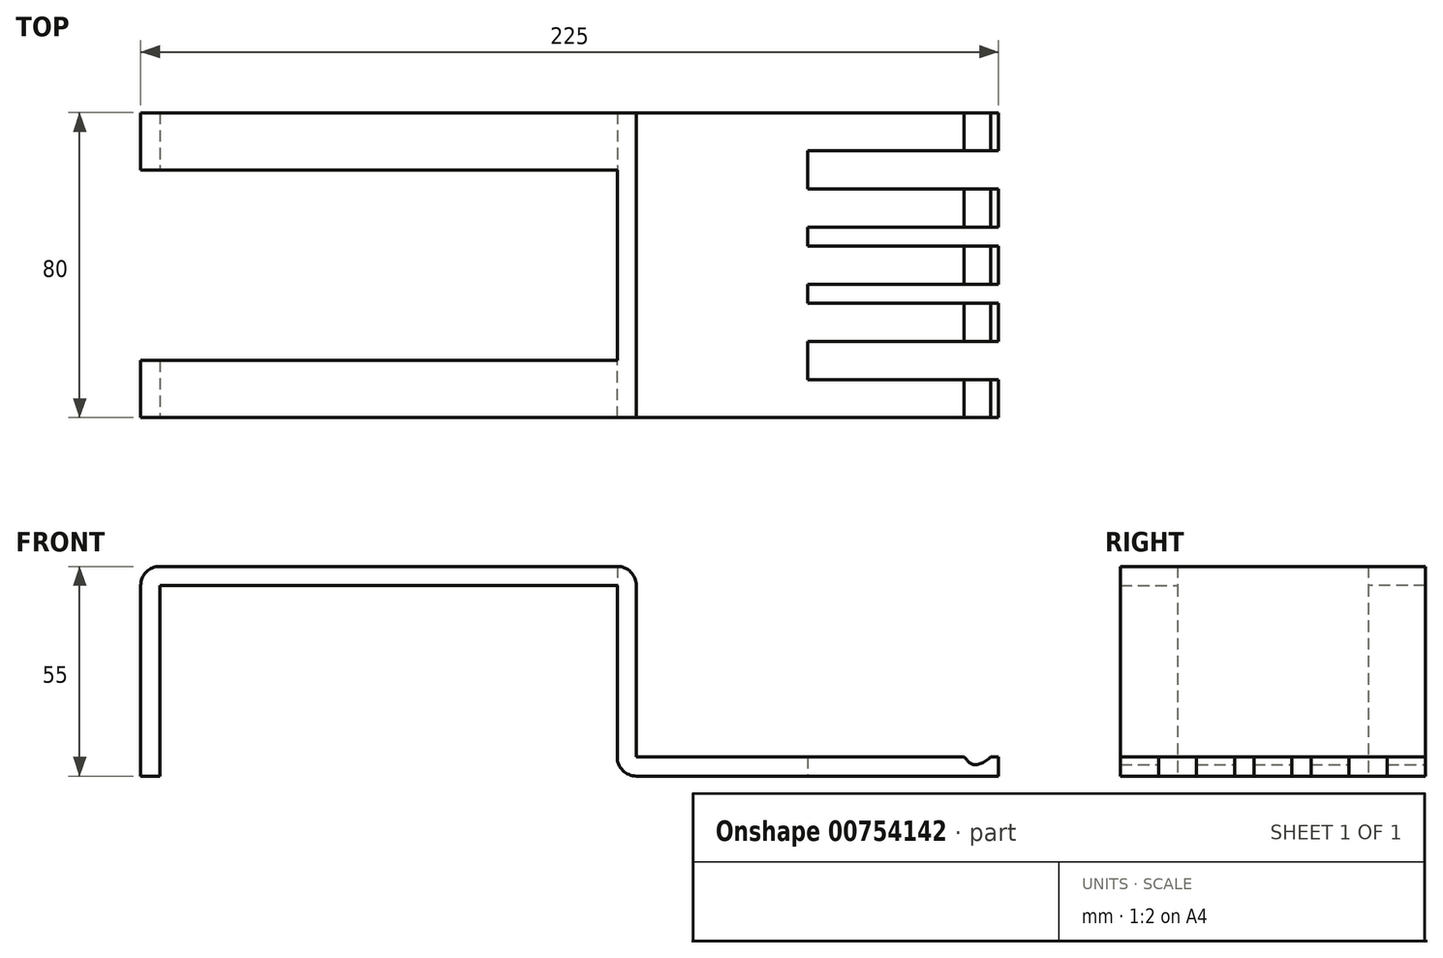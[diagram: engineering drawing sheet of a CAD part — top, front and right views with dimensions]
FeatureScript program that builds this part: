
annotation { "Feature Type Name" : "Feature", "Feature Type Description" : "" }
export const myFeature = defineFeature(function(context is Context, id is Id, definition is map)
    precondition{}
    {
        {
            var Q0;
            Q0=qCreatedBy(makeId("Top.planeOp"),FACE);
            var sketch = newSketch(context, id + "F0", { "sketchPlane" : qUnion([Q0])});
            skLineSegment(sketch, "E0.bottom", {"start": v(9.87, 39.42) * mm, "end": v(109.87, 39.42) * mm});
            skLineSegment(sketch, "E0.top", {"start": v(9.87, -40.58) * mm, "end": v(109.87, -40.58) * mm});
            skLineSegment(sketch, "E0.left", {"start": v(9.87, 39.42) * mm, "end": v(9.87, -40.58) * mm});
            skLineSegment(sketch, "E0.right", {"start": v(109.87, 39.42) * mm, "end": v(109.87, -40.58) * mm});
            skLineSegment(sketch, "E1", {"start": v(59.87, 39.42) * mm, "end": v(59.87, -40.58) * mm, "construction": true});
            skLineSegment(sketch, "E2.bottom", {"start": v(9.87, 39.42) * mm, "end": v(14.87, 39.42) * mm});
            skLineSegment(sketch, "E2.top", {"start": v(9.87, -40.58) * mm, "end": v(14.87, -40.58) * mm});
            skLineSegment(sketch, "E2.right", {"start": v(14.87, 39.42) * mm, "end": v(14.87, -40.58) * mm});
            skLineSegment(sketch, "E3.bottom", {"start": v(59.87, 29.42) * mm, "end": v(109.87, 29.42) * mm});
            skLineSegment(sketch, "E3.top", {"start": v(59.87, 19.42) * mm, "end": v(109.87, 19.42) * mm});
            skLineSegment(sketch, "E3.left", {"start": v(59.87, 29.42) * mm, "end": v(59.87, 19.42) * mm});
            skLineSegment(sketch, "E3.right", {"start": v(109.87, 29.42) * mm, "end": v(109.87, 19.42) * mm});
            skLineSegment(sketch, "E4.bottom", {"start": v(59.87, 9.42) * mm, "end": v(109.87, 9.42) * mm});
            skLineSegment(sketch, "E4.top", {"start": v(59.87, 4.42) * mm, "end": v(109.87, 4.42) * mm});
            skLineSegment(sketch, "E4.left", {"start": v(59.87, 9.42) * mm, "end": v(59.87, 4.42) * mm});
            skLineSegment(sketch, "E4.right", {"start": v(109.87, 9.42) * mm, "end": v(109.87, 4.42) * mm});
            skLineSegment(sketch, "E5.bottom", {"start": v(59.87, -20.58) * mm, "end": v(109.87, -20.58) * mm});
            skLineSegment(sketch, "E5.top", {"start": v(59.87, -30.58) * mm, "end": v(109.87, -30.58) * mm});
            skLineSegment(sketch, "E5.left", {"start": v(59.87, -20.58) * mm, "end": v(59.87, -30.58) * mm});
            skLineSegment(sketch, "E5.right", {"start": v(109.87, -20.58) * mm, "end": v(109.87, -30.58) * mm});
            skLineSegment(sketch, "E6.bottom", {"start": v(14.87, 39.42) * mm, "end": v(59.87, 39.42) * mm});
            skLineSegment(sketch, "E6.top", {"start": v(14.87, -40.58) * mm, "end": v(59.87, -40.58) * mm});
            skLineSegment(sketch, "E6.right", {"start": v(59.87, 39.42) * mm, "end": v(59.87, -40.58) * mm});
            skLineSegment(sketch, "E7.bottom", {"start": v(59.87, -5.58) * mm, "end": v(109.87, -5.58) * mm});
            skLineSegment(sketch, "E7.top", {"start": v(59.87, -10.58) * mm, "end": v(109.87, -10.58) * mm});
            skLineSegment(sketch, "E7.left", {"start": v(59.87, -5.58) * mm, "end": v(59.87, -10.58) * mm});
            skLineSegment(sketch, "E7.right", {"start": v(109.87, -5.58) * mm, "end": v(109.87, -10.58) * mm});
            skSolve(sketch);
        }
        {
            var Q0;
            {var subQ8=sQuery(id+"F0.wireOp",EDGE,"E2.right");Q0=makeQuery(id+"F0.imprint","IMPRINT",FACE,{"disambiguationData":[TD([[makeQuery(id+"F0.imprint","IMPRINT",EDGE,{"derivedFrom":subQ8}),1.0]])]});}
            var Q1;
            {var subQ0=sQuery(id+"F0.wireOp",EDGE,"E4.top");Q1=makeQuery(id+"F0.imprint","IMPRINT",FACE,{"disambiguationData":[TD([[makeQuery(id+"F0.imprint","IMPRINT",EDGE,{"derivedFrom":subQ0}),-1.0]])]});}
            var Q2;
            {var subQ5=sQuery(id+"F0.wireOp",EDGE,"E5.top");Q2=makeQuery(id+"F0.imprint","IMPRINT",FACE,{"disambiguationData":[TD([[makeQuery(id+"F0.imprint","IMPRINT",EDGE,{"derivedFrom":subQ5}),-1.0]])]});}
            var Q3;
            {var subQ0=sQuery(id+"F0.wireOp",EDGE,"E3.top");Q3=makeQuery(id+"F0.imprint","IMPRINT",FACE,{"disambiguationData":[TD([[makeQuery(id+"F0.imprint","IMPRINT",EDGE,{"derivedFrom":subQ0}),-1.0]])]});}
            var Q4;
            {var subQ5=sQuery(id+"F0.wireOp",EDGE,"E3.bottom");Q4=makeQuery(id+"F0.imprint","IMPRINT",FACE,{"disambiguationData":[TD([[makeQuery(id+"F0.imprint","IMPRINT",EDGE,{"derivedFrom":subQ5}),1.0]])]});}
            var Q5;
            {var subQ0=sQuery(id+"F0.wireOp",EDGE,"E5.bottom");Q5=makeQuery(id+"F0.imprint","IMPRINT",FACE,{"disambiguationData":[TD([[makeQuery(id+"F0.imprint","IMPRINT",EDGE,{"derivedFrom":subQ0}),1.0]])]});}
            extrude(context, id + "F1", {"entities" : qUnion([Q0, Q1, Q2, Q3, Q4, Q5]), "depth" : 5 * mm, "offsetDistance" : 25 * mm});
        }
        {
            var Q0;
            {var subQ2=sQuery(id+"F0.wireOp",EDGE,"E0.left");Q0=makeQuery(id+"F0.imprint","IMPRINT",FACE,{"disambiguationData":[TD([[makeQuery(id+"F0.imprint","IMPRINT",EDGE,{"derivedFrom":subQ2}),1.0]])]});}
            extrude(context, id + "F2", {"entities" : qUnion([Q0]), "operationType" : NewBodyOperationType.ADD, "depth" : 55 * mm, "offsetDistance" : 25 * mm});
        }
        {
            var Q0;
            Q0=makeQuery(id+"F2.opExtrude","SWEPT_FACE",FACE,{"disambiguationData":[OSD([sQuery(id+"F0.wireOp",EDGE,"E0.left")])]});
            var sketch = newSketch(context, id + "F3", { "sketchPlane" : qUnion([Q0])});
            skLineSegment(sketch, "E8.bottom", {"start": v(-39.42, 55) * mm, "end": v(-24.42, 55) * mm});
            skLineSegment(sketch, "E8.top", {"start": v(-39.42, 50) * mm, "end": v(-24.42, 50) * mm});
            skLineSegment(sketch, "E8.left", {"start": v(-39.42, 55) * mm, "end": v(-39.42, 50) * mm});
            skLineSegment(sketch, "E8.right", {"start": v(-24.42, 55) * mm, "end": v(-24.42, 50) * mm});
            skLineSegment(sketch, "E9.bottom", {"start": v(40.58, 55) * mm, "end": v(25.58, 55) * mm});
            skLineSegment(sketch, "E9.top", {"start": v(40.58, 50) * mm, "end": v(25.58, 50) * mm});
            skLineSegment(sketch, "E9.left", {"start": v(40.58, 55) * mm, "end": v(40.58, 50) * mm});
            skLineSegment(sketch, "E9.right", {"start": v(25.58, 55) * mm, "end": v(25.58, 50) * mm});
            skSolve(sketch);
        }
        {
            var Q0;
            Q0=makeQuery(id+"F3.imprint","IMPRINT",FACE,{"disambiguationData":[TD([[makeQuery(id+"F3.imprint","IMPRINT",EDGE,{"derivedFrom":sQuery(id+"F3.wireOp",EDGE,"E8.bottom")}),-1.0]])]});
            var Q1;
            Q1=makeQuery(id+"F3.imprint","IMPRINT",FACE,{"disambiguationData":[TD([[makeQuery(id+"F3.imprint","IMPRINT",EDGE,{"derivedFrom":sQuery(id+"F3.wireOp",EDGE,"E9.bottom")}),-1.0]])]});
            extrude(context, id + "F4", {"entities" : qUnion([Q0, Q1]), "operationType" : NewBodyOperationType.ADD, "depth" : 125 * mm, "offsetDistance" : 25 * mm});
        }
        {
            var Q0;
            Q0=makeQuery(id+"F4.opExtrude","SWEPT_FACE",FACE,{"disambiguationData":[OSD([sQuery(id+"F3.wireOp",EDGE,"E8.top")])]});
            var sketch = newSketch(context, id + "F5", { "sketchPlane" : qUnion([Q0])});
            skLineSegment(sketch, "E10.bottom", {"start": v(-115.13, -39.42) * mm, "end": v(-110.13, -39.42) * mm});
            skLineSegment(sketch, "E10.top", {"start": v(-115.13, -24.42) * mm, "end": v(-110.13, -24.42) * mm});
            skLineSegment(sketch, "E10.left", {"start": v(-115.13, -39.42) * mm, "end": v(-115.13, -24.42) * mm});
            skLineSegment(sketch, "E10.right", {"start": v(-110.13, -39.42) * mm, "end": v(-110.13, -24.42) * mm});
            skSolve(sketch);
        }
        {
            var Q0;
            Q0=makeQuery(id+"F4.opExtrude","SWEPT_FACE",FACE,{"disambiguationData":[OSD([sQuery(id+"F3.wireOp",EDGE,"E9.top")])]});
            var sketch = newSketch(context, id + "F6", { "sketchPlane" : qUnion([Q0])});
            skLineSegment(sketch, "E11.bottom", {"start": v(-115.13, 25.58) * mm, "end": v(-110.13, 25.58) * mm});
            skLineSegment(sketch, "E11.top", {"start": v(-115.13, 40.58) * mm, "end": v(-110.13, 40.58) * mm});
            skLineSegment(sketch, "E11.left", {"start": v(-115.13, 25.58) * mm, "end": v(-115.13, 40.58) * mm});
            skLineSegment(sketch, "E11.right", {"start": v(-110.13, 25.58) * mm, "end": v(-110.13, 40.58) * mm});
            skSolve(sketch);
        }
        {
            var Q0;
            Q0=makeQuery(id+"F6.imprint","IMPRINT",FACE,{"disambiguationData":[TD([[makeQuery(id+"F6.imprint","IMPRINT",EDGE,{"derivedFrom":sQuery(id+"F6.wireOp",EDGE,"E11.bottom")}),1.0]])]});
            var Q1;
            Q1=makeQuery(id+"F5.imprint","IMPRINT",FACE,{"disambiguationData":[TD([[makeQuery(id+"F5.imprint","IMPRINT",EDGE,{"derivedFrom":sQuery(id+"F5.wireOp",EDGE,"E10.bottom")}),1.0]])]});
            extrude(context, id + "F7", {"entities" : qUnion([Q0, Q1]), "operationType" : NewBodyOperationType.ADD, "depth" : 50 * mm, "offsetDistance" : 25 * mm});
        }
        {
            var Q0;
            Q0=makeQuery(id+"F4.opExtrude","CAP_EDGE",EDGE,{"disambiguationData":[OSD([sQuery(id+"F3.wireOp",EDGE,"E8.bottom")])],"isStart":false});
            var Q1;
            Q1=makeQuery(id+"F4.opExtrude","CAP_EDGE",EDGE,{"disambiguationData":[OSD([sQuery(id+"F3.wireOp",EDGE,"E9.bottom")])],"isStart":false});
            var Q2;
            Q2=makeQuery(id+"F2.opExtrude","CAP_EDGE",EDGE,{"disambiguationData":[OSD([sQuery(id+"F0.wireOp",EDGE,"E0.left")])],"isStart":true});
            var Q3;
            Q3=makeQuery(id+"F2.opExtrude","CAP_EDGE",EDGE,{"disambiguationData":[OSD([sQuery(id+"F0.wireOp",EDGE,"E2.right")])],"isStart":false});
            fillet(context, id + "F8", {"entities" : qUnion([Q0, Q1, Q2, Q3]), "radius" : 5 * mm, "tangentPropagation" : true, "allowEdgeOverflow" : false});
        }
        {
            var Q0;
            {var subQ0=sQuery(id+"F0.wireOp",EDGE,"E0.top");Q0=makeQuery(id+"F7.boolean.opBoolean","MERGE",FACE,{"derivedFrom":[makeQuery(id+"F4.boolean.opBoolean","MERGE",FACE,{"derivedFrom":[makeQuery(id+"F2.boolean.opBoolean","MERGE",FACE,{"derivedFrom":[makeQuery(id+"F1.opExtrude","SWEPT_FACE",FACE,{"disambiguationData":[OSD([subQ0])]}),makeQuery(id+"F2.opExtrude","SWEPT_FACE",FACE,{"disambiguationData":[OSD([subQ0])]})]}),makeQuery(id+"F4.opExtrude","SWEPT_FACE",FACE,{"disambiguationData":[OSD([sQuery(id+"F3.wireOp",EDGE,"E9.left")])]})]}),makeQuery(id+"F7.opExtrude","SWEPT_FACE",FACE,{"disambiguationData":[OSD([sQuery(id+"F6.wireOp",EDGE,"E11.top")])]})]});}
            var sketch = newSketch(context, id + "F9", { "sketchPlane" : qUnion([Q0])});
            skFitSpline(sketch, "E12", {"points": [v(107.87, 5) * mm, v(103.37, 3) * mm, v(100.87, 5) * mm], "startDerivative": vector(-6, -6.37) * mm, "endDerivative": vector(-5.84, 6.2) * mm});
            skSolve(sketch);
        }
        {
            var Q0;
            {var subQ0=sQuery(id+"F9.wireOp",EDGE,"E12");Q0=makeQuery(id+"F9.imprint","IMPRINT",FACE,{"disambiguationData":[TD([[makeQuery(id+"F9.imprint","IMPRINT",EDGE,{"derivedFrom":subQ0}),-1.0]])]});}
            extrude(context, id + "F10", {"entities" : qUnion([Q0]), "operationType" : NewBodyOperationType.REMOVE, "endBound" : BoundingType.THROUGH_ALL, "oppositeDirection" : true, "depth" : 25 * mm, "offsetDistance" : 25 * mm});
        }
    });
